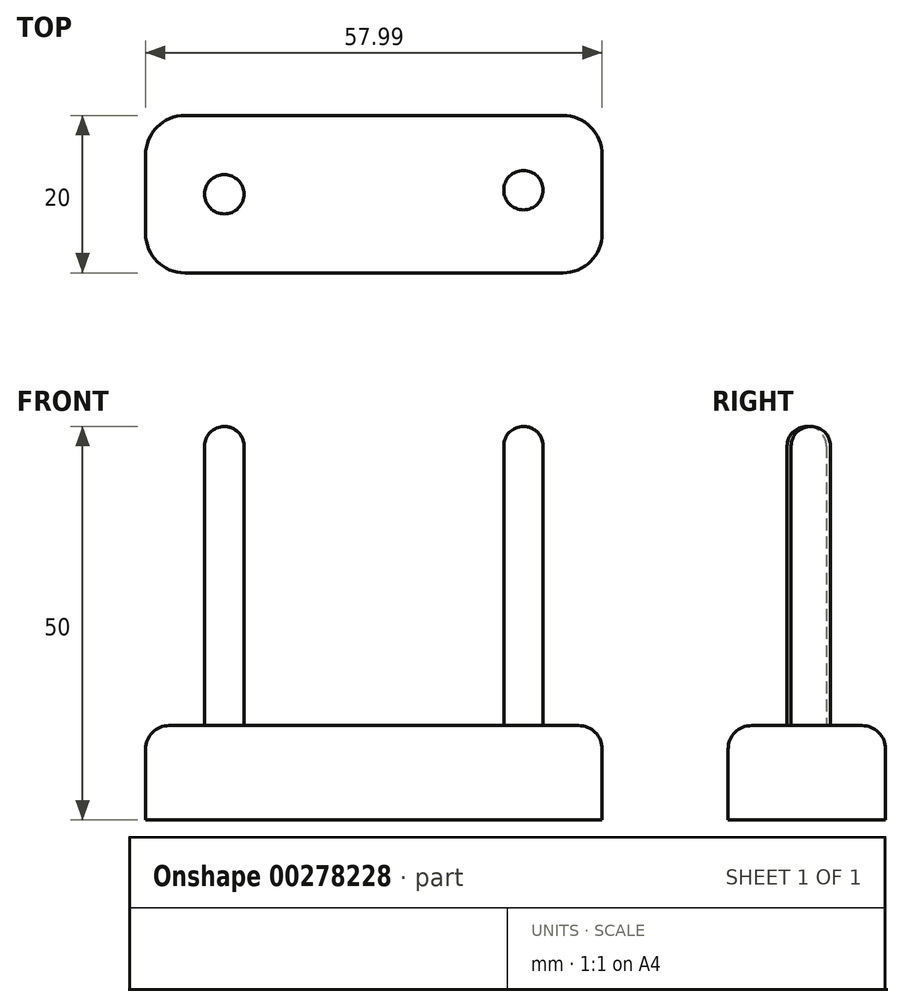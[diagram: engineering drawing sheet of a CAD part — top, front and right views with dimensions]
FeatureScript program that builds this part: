
annotation { "Feature Type Name" : "Feature", "Feature Type Description" : "" }
export const myFeature = defineFeature(function(context is Context, id is Id, definition is map)
    precondition{}
    {
        {
            var Q0;
            Q0=qCreatedBy(makeId("Top.planeOp"),FACE);
            var sketch = newSketch(context, id + "F0", { "sketchPlane" : qUnion([Q0])});
            skCircle(sketch, "E0", {"center": v(-16.96, 27.82) * mm, "radius": 2.5 * mm});
            skCircle(sketch, "E1", {"center": v(21.03, 28.34) * mm, "radius": 2.5 * mm});
            skLineSegment(sketch, "E2.bottom", {"start": v(-26.96, 37.82) * mm, "end": v(31.03, 37.82) * mm});
            skLineSegment(sketch, "E2.top", {"start": v(-26.96, 17.82) * mm, "end": v(31.03, 17.82) * mm});
            skLineSegment(sketch, "E2.left", {"start": v(-26.96, 37.82) * mm, "end": v(-26.96, 17.82) * mm});
            skLineSegment(sketch, "E2.right", {"start": v(31.03, 37.82) * mm, "end": v(31.03, 17.82) * mm});
            skSolve(sketch);
        }
        {
            var Q0;
            Q0=makeQuery(id+"F0.imprint","IMPRINT",FACE,{"disambiguationData":[TD([[makeQuery(id+"F0.imprint","IMPRINT",EDGE,{"derivedFrom":sQuery(id+"F0.wireOp",EDGE,"E0")}),-1.0]])]});
            var Q1;
            Q1=makeQuery(id+"F0.imprint","IMPRINT",FACE,{"disambiguationData":[TD([[makeQuery(id+"F0.imprint","IMPRINT",EDGE,{"derivedFrom":sQuery(id+"F0.wireOp",EDGE,"E0")}),1.0]])]});
            var Q2;
            Q2=makeQuery(id+"F0.imprint","IMPRINT",FACE,{"disambiguationData":[TD([[makeQuery(id+"F0.imprint","IMPRINT",EDGE,{"derivedFrom":sQuery(id+"F0.wireOp",EDGE,"E1")}),1.0]])]});
            extrude(context, id + "F1", {"entities" : qUnion([Q0, Q1, Q2]), "depth" : 12 * mm});
        }
        {
            var Q0;
            Q0=makeQuery(id+"F0.imprint","IMPRINT",FACE,{"disambiguationData":[TD([[makeQuery(id+"F0.imprint","IMPRINT",EDGE,{"derivedFrom":sQuery(id+"F0.wireOp",EDGE,"E0")}),1.0]])]});
            var Q1;
            Q1=makeQuery(id+"F0.imprint","IMPRINT",FACE,{"disambiguationData":[TD([[makeQuery(id+"F0.imprint","IMPRINT",EDGE,{"derivedFrom":sQuery(id+"F0.wireOp",EDGE,"E1")}),1.0]])]});
            extrude(context, id + "F2", {"entities" : qUnion([Q0, Q1]), "operationType" : NewBodyOperationType.ADD, "depth" : 50 * mm});
        }
        {
            var Q0;
            Q0=makeQuery(id+"F2.opExtrude","CAP_EDGE",EDGE,{"disambiguationData":[OSD([sQuery(id+"F0.wireOp",EDGE,"E0")])],"isStart":false});
            var Q1;
            Q1=makeQuery(id+"F2.opExtrude","CAP_EDGE",EDGE,{"disambiguationData":[OSD([sQuery(id+"F0.wireOp",EDGE,"E1")])],"isStart":false});
            fillet(context, id + "F3", {"entities" : qUnion([Q0, Q1]), "radius" : 2.5 * mm, "tangentPropagation" : true, "allowEdgeOverflow" : false});
        }
        {
            var Q0;
            Q0=makeQuery(id+"F1.opExtrude","SWEPT_EDGE",EDGE,{"disambiguationData":[OSD([sQuery(id+"F0.wireOp",EDGE,"E2.bottom"),sQuery(id+"F0.wireOp",EDGE,"E2.left")])]});
            var Q1;
            Q1=makeQuery(id+"F1.opExtrude","SWEPT_EDGE",EDGE,{"disambiguationData":[OSD([sQuery(id+"F0.wireOp",EDGE,"E2.top"),sQuery(id+"F0.wireOp",EDGE,"E2.left")])]});
            var Q2;
            Q2=makeQuery(id+"F1.opExtrude","SWEPT_EDGE",EDGE,{"disambiguationData":[OSD([sQuery(id+"F0.wireOp",EDGE,"E2.top"),sQuery(id+"F0.wireOp",EDGE,"E2.right")])]});
            var Q3;
            Q3=makeQuery(id+"F1.opExtrude","SWEPT_EDGE",EDGE,{"disambiguationData":[OSD([sQuery(id+"F0.wireOp",EDGE,"E2.bottom"),sQuery(id+"F0.wireOp",EDGE,"E2.right")])]});
            fillet(context, id + "F4", {"entities" : qUnion([Q0, Q1, Q2, Q3]), "radius" : 5 * mm, "tangentPropagation" : true, "allowEdgeOverflow" : false});
        }
        {
            var Q0;
            Q0=makeQuery(id+"F1.opExtrude","CAP_EDGE",EDGE,{"disambiguationData":[OSD([sQuery(id+"F0.wireOp",EDGE,"E2.bottom")])],"isStart":false});
            fillet(context, id + "F5", {"entities" : qUnion([Q0]), "radius" : 3 * mm, "tangentPropagation" : true, "allowEdgeOverflow" : false});
        }
    });
